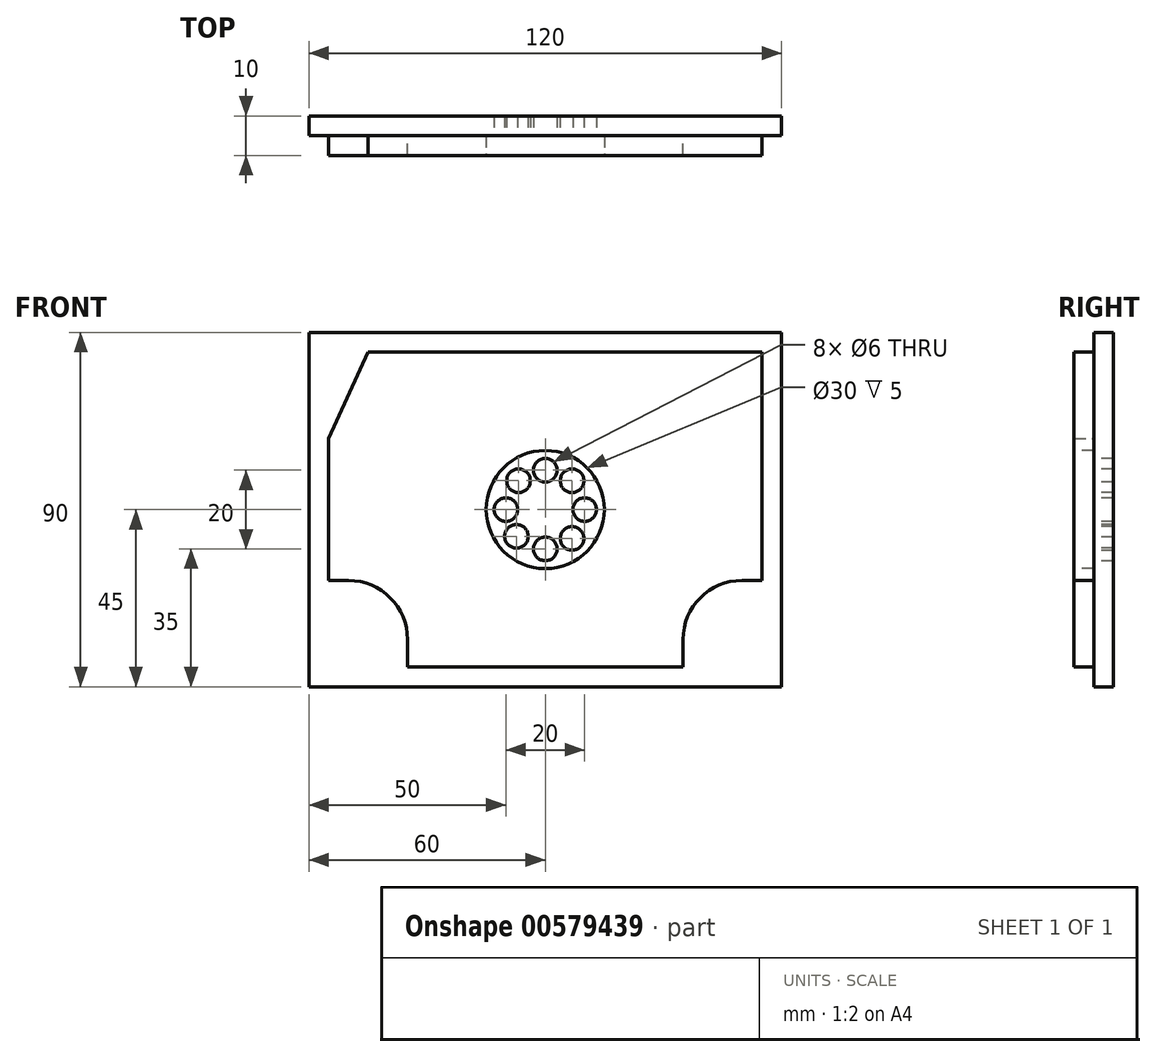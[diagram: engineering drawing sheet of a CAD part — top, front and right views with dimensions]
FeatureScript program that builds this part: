
annotation { "Feature Type Name" : "Feature", "Feature Type Description" : "" }
export const myFeature = defineFeature(function(context is Context, id is Id, definition is map)
    precondition{}
    {
        {
            var Q0;
            Q0=qCreatedBy(makeId("Front.planeOp"),FACE);
            var sketch = newSketch(context, id + "F0", { "sketchPlane" : qUnion([Q0])});
            skLineSegment(sketch, "E0.bottom", {"start": v(-60, 45) * mm, "end": v(60, 45) * mm});
            skLineSegment(sketch, "E0.top", {"start": v(-60, -45) * mm, "end": v(60, -45) * mm});
            skLineSegment(sketch, "E0.left", {"start": v(-60, 45) * mm, "end": v(-60, -45) * mm});
            skLineSegment(sketch, "E0.right", {"start": v(60, 45) * mm, "end": v(60, -45) * mm});
            skPoint(sketch, "E0.middle", {"position": v(0, 0) * mm});
            skSolve(sketch);
        }
        {
            var Q0;
            Q0=makeQuery(id+"F0.imprint","IMPRINT",FACE,{"disambiguationData":[TD([[makeQuery(id+"F0.imprint","IMPRINT",EDGE,{"derivedFrom":sQuery(id+"F0.wireOp",EDGE,"E0.bottom")}),-1.0]])]});
            extrude(context, id + "F1", {"entities" : qUnion([Q0]), "depth" : 5 * mm, "offsetDistance" : 25 * mm});
        }
        {
            var Q0;
            Q0=makeQuery(id+"F1.opExtrude","CAP_FACE",FACE,{"disambiguationData":[OSD([sQuery(id+"F0.wireOp",EDGE,"E0.bottom"),sQuery(id+"F0.wireOp",EDGE,"E0.top"),sQuery(id+"F0.wireOp",EDGE,"E0.left"),sQuery(id+"F0.wireOp",EDGE,"E0.right")])],"isStart":false});
            var sketch = newSketch(context, id + "F2", { "sketchPlane" : qUnion([Q0])});
            skLineSegment(sketch, "E1", {"start": v(55, 40) * mm, "end": v(-45, 40) * mm});
            skLineSegment(sketch, "E2", {"start": v(-45, 40) * mm, "end": v(-55, 18) * mm});
            skLineSegment(sketch, "E3", {"start": v(-55, 18) * mm, "end": v(-55, -18) * mm});
            skLineSegment(sketch, "E4", {"start": v(-55, -18) * mm, "end": v(-50, -18) * mm});
            skLineSegment(sketch, "E5", {"start": v(-35, -33) * mm, "end": v(-35, -40) * mm});
            skLineSegment(sketch, "E6", {"start": v(-35, -40) * mm, "end": v(35, -40) * mm});
            skLineSegment(sketch, "E7", {"start": v(35, -40) * mm, "end": v(35, -33) * mm});
            skLineSegment(sketch, "E8", {"start": v(50, -18) * mm, "end": v(55, -18) * mm});
            skLineSegment(sketch, "E9", {"start": v(55, -18) * mm, "end": v(55, 40) * mm});
            skPoint(sketch, "E10.visualSharp", {"position": v(-35, -18) * mm});
            skArc(sketch, "E10.filletArc", {"start": v(-35, -33) * mm, "mid": v(-39.4, -22.4) * mm, "end": v(-50, -18) * mm});
            skPoint(sketch, "E11.visualSharp", {"position": v(35, -18) * mm});
            skArc(sketch, "E11.filletArc", {"start": v(50, -18) * mm, "mid": v(39.4, -22.4) * mm, "end": v(35, -33) * mm});
            skSolve(sketch);
        }
        {
            var Q0;
            Q0=makeQuery(id+"F2.imprint","IMPRINT",FACE,{"disambiguationData":[TD([[makeQuery(id+"F2.imprint","IMPRINT",EDGE,{"derivedFrom":sQuery(id+"F2.wireOp",EDGE,"E1")}),1.0]])]});
            extrude(context, id + "F3", {"entities" : qUnion([Q0]), "operationType" : NewBodyOperationType.ADD, "depth" : 5 * mm, "offsetDistance" : 25 * mm});
        }
        {
            var Q0;
            Q0=makeQuery(id+"F3.opExtrude","CAP_FACE",FACE,{"disambiguationData":[OSD([sQuery(id+"F2.wireOp",EDGE,"E1"),sQuery(id+"F2.wireOp",EDGE,"E2"),sQuery(id+"F2.wireOp",EDGE,"E3"),sQuery(id+"F2.wireOp",EDGE,"E4"),sQuery(id+"F2.wireOp",EDGE,"E5"),sQuery(id+"F2.wireOp",EDGE,"E6"),sQuery(id+"F2.wireOp",EDGE,"E7"),sQuery(id+"F2.wireOp",EDGE,"E8"),sQuery(id+"F2.wireOp",EDGE,"E9"),sQuery(id+"F2.wireOp",EDGE,"E10.filletArc"),sQuery(id+"F2.wireOp",EDGE,"E11.filletArc")])],"isStart":false});
            var sketch = newSketch(context, id + "F4", { "sketchPlane" : qUnion([Q0])});
            skCircle(sketch, "E12", {"center": v(0, 0) * mm, "radius": 15 * mm});
            skSolve(sketch);
        }
        {
            var Q0;
            Q0=makeQuery(id+"F4.imprint","IMPRINT",FACE,{"disambiguationData":[TD([[makeQuery(id+"F4.imprint","IMPRINT",EDGE,{"derivedFrom":sQuery(id+"F4.wireOp",EDGE,"E12")}),1.0]])]});
            extrude(context, id + "F5", {"entities" : qUnion([Q0]), "operationType" : NewBodyOperationType.REMOVE, "oppositeDirection" : true, "depth" : 5 * mm, "offsetDistance" : 25 * mm});
        }
        {
            var Q0;
            Q0=makeQuery(id+"F5.boolean.opBoolean","COPY",FACE,{"derivedFrom":makeQuery(id+"F5.opExtrude","CAP_FACE",FACE,{"disambiguationData":[OSD([sQuery(id+"F4.wireOp",EDGE,"E12")])],"isStart":false})});
            var sketch = newSketch(context, id + "F6", { "sketchPlane" : qUnion([Q0])});
            skCircle(sketch, "E13", {"center": v(0, 10) * mm, "radius": 3 * mm});
            skCircle(sketch, "E14", {"center": v(0, -10) * mm, "radius": 3 * mm});
            skCircle(sketch, "E15", {"center": v(10, 0) * mm, "radius": 3 * mm});
            skCircle(sketch, "E16", {"center": v(-10, 0) * mm, "radius": 3 * mm});
            skCircle(sketch, "E17", {"center": v(-7.33, -6.8) * mm, "radius": 3 * mm});
            skCircle(sketch, "E18", {"center": v(-6.8, 7.33) * mm, "radius": 3 * mm});
            skCircle(sketch, "E19", {"center": v(6.8, 7.33) * mm, "radius": 3 * mm});
            skCircle(sketch, "E20", {"center": v(6.8, -7.33) * mm, "radius": 3 * mm});
            skSolve(sketch);
        }
        {
            var Q0;
            Q0=makeQuery(id+"F6.imprint","IMPRINT",FACE,{"disambiguationData":[TD([[makeQuery(id+"F6.imprint","IMPRINT",EDGE,{"derivedFrom":sQuery(id+"F6.wireOp",EDGE,"E13")}),1.0]])]});
            var Q1;
            Q1=makeQuery(id+"F6.imprint","IMPRINT",FACE,{"disambiguationData":[TD([[makeQuery(id+"F6.imprint","IMPRINT",EDGE,{"derivedFrom":sQuery(id+"F6.wireOp",EDGE,"E18")}),1.0]])]});
            var Q2;
            Q2=makeQuery(id+"F6.imprint","IMPRINT",FACE,{"disambiguationData":[TD([[makeQuery(id+"F6.imprint","IMPRINT",EDGE,{"derivedFrom":sQuery(id+"F6.wireOp",EDGE,"E16")}),1.0]])]});
            var Q3;
            Q3=makeQuery(id+"F6.imprint","IMPRINT",FACE,{"disambiguationData":[TD([[makeQuery(id+"F6.imprint","IMPRINT",EDGE,{"derivedFrom":sQuery(id+"F6.wireOp",EDGE,"E17")}),1.0]])]});
            var Q4;
            Q4=makeQuery(id+"F6.imprint","IMPRINT",FACE,{"disambiguationData":[TD([[makeQuery(id+"F6.imprint","IMPRINT",EDGE,{"derivedFrom":sQuery(id+"F6.wireOp",EDGE,"E14")}),1.0]])]});
            var Q5;
            Q5=makeQuery(id+"F6.imprint","IMPRINT",FACE,{"disambiguationData":[TD([[makeQuery(id+"F6.imprint","IMPRINT",EDGE,{"derivedFrom":sQuery(id+"F6.wireOp",EDGE,"E20")}),1.0]])]});
            var Q6;
            Q6=makeQuery(id+"F6.imprint","IMPRINT",FACE,{"disambiguationData":[TD([[makeQuery(id+"F6.imprint","IMPRINT",EDGE,{"derivedFrom":sQuery(id+"F6.wireOp",EDGE,"E15")}),1.0]])]});
            var Q7;
            Q7=makeQuery(id+"F6.imprint","IMPRINT",FACE,{"disambiguationData":[TD([[makeQuery(id+"F6.imprint","IMPRINT",EDGE,{"derivedFrom":sQuery(id+"F6.wireOp",EDGE,"E19")}),1.0]])]});
            extrude(context, id + "F7", {"entities" : qUnion([Q0, Q1, Q2, Q3, Q4, Q5, Q6, Q7]), "operationType" : NewBodyOperationType.REMOVE, "oppositeDirection" : true, "depth" : 5 * mm, "offsetDistance" : 25 * mm});
        }
    });
